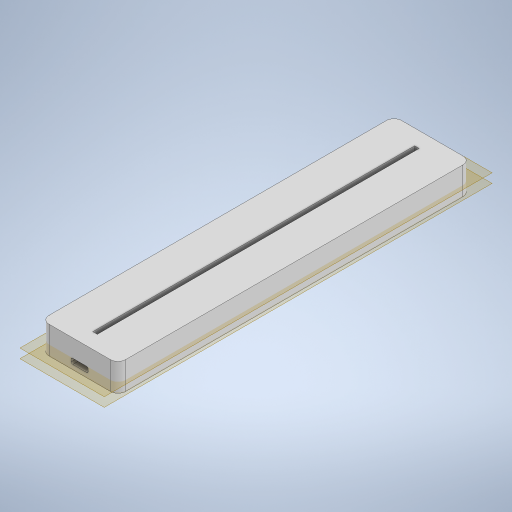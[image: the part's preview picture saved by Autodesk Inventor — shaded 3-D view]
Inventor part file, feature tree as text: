
AUTODESK INVENTOR PART (.ipt)
format: ipt  version: 2024 (Build 280153000, 153)  size: 304,640 bytes
history: native  units: in
note: dims shown in document units (in); Inventor stores cm internally (conversion verified against a paired STEP export)
features: extrude x5, sketch x4, plane x2, direct_edit x1, move_body x1
ambient origin geometry x8: Origin, YZ Plane, XZ Plane, XY Plane, X Axis, Y Axis, Z Axis, Center Point
bodies: Solid1 (feature_tree)
feature tree (13):
  sketch  "Sketch1"  dims[d6=0.3937in d7=8.2677in]
  extrude  "Extrusion1"  Depth=8.2677in
  extrude  "Extrusion2"  Depth=0.1181in
  sketch  "Sketch2"  dims[d8=0.1969in d9=0.1181in]
  extrude  "Extrusion3"  Depth=1.1811in TaperAngle=0.0deg
  extrude  "Extrusion4"  Depth=0.1181in
  plane  "Work Plane1"
  extrude  "Extrusion5"  Depth=8.2677in
  plane  "Work Plane2"
  direct_edit  "Direct Edit1"
  sketch  "Sketch5"  dims[d10=8.2677in d11=1.1811in d12=0.0in]
  sketch  "Sketch6"  dims[d13=0.5906in d14=0.0in d15=0.1181in d16=8.2677in d17=0.5906in d18=0.0in d23=0.4331in d24=0.1378in d27=0.0394in d28=8.8583in d29=0.0in d30=-0.4528in d31=0.1378in d32=0.1772in d33=0.0in d34=-0.2362in d35=0.0in d36=0.0in d37=-0.4724in d38=0.7677in d19=0.0197in d20=0.0344in d21=0.0197in d22=0.0344in]
  move_body  "Move1"
